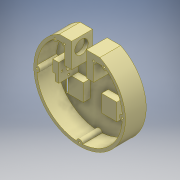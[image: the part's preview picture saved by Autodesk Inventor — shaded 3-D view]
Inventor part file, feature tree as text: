
AUTODESK INVENTOR PART (.ipt)
format: ipt  version: 2016 (Build 200138000, 138)  size: 337,920 bytes
history: native  units: mm
features: extrude x13, sketch x13, other x1
ambient origin geometry x8: Origin, YZ Plane, XZ Plane, XY Plane, X Axis, Y Axis, Z Axis, Center Point
bodies: Body1 (feature_tree)
feature tree (27):
  other  "Sólido1"
  extrude  "Extrusión1"  Depth=18.0mm
  extrude  "Extrusión2"  Depth=15.0mm
  extrude  "Extrusión3"  Depth=15.0mm
  extrude  "Extrusión4"  Depth=40.0mm
  extrude  "Extrusión5"  Depth=2.0mm TaperAngle=0.0deg
  extrude  "Extrusión6"  Depth=140.0mm
  extrude  "Extrusión8"  Depth=25.0mm
  extrude  "Extrusión9"  Depth=25.0mm
  extrude  "Extrusión10"  Depth=11.0mm TaperAngle=0.0deg
  extrude  "Extrusión11"  Depth=32.0mm TaperAngle=0.0deg
  extrude  "Extrusión12"  Depth=22.0mm
  extrude  "Extrusión13"  Depth=38.0mm TaperAngle=0.0deg
  extrude  "Extrusión14"  Depth=10.0mm
  sketch  "Boceto1"  dims[d0=150.0mm d2=18.0mm]
  sketch  "Boceto2"  dims[d3=25.0mm d4=15.0mm]
  sketch  "Boceto3"  dims[d5=50.0mm d6=15.0mm]
  sketch  "Boceto4"  dims[d7=50.0mm d8=40.0mm]
  sketch  "Boceto5"  dims[d9=40.0mm d12=2.0mm d13=0.0mm]
  sketch  "Boceto6"  dims[d14=150.0mm d23=140.0mm]
  sketch  "Boceto8"  dims[d25=32.0mm d26=0.0mm d27=25.0mm]
  sketch  "Boceto9"  dims[d28=28.0mm d30=25.0mm]
  sketch  "Boceto10"  dims[d31=28.0mm d33=11.0mm d34=0.0mm]
  sketch  "Boceto11"  dims[d37=21.0mm d38=32.0mm d39=0.0mm]
  sketch  "Boceto12"  dims[d40=22.0mm d41=21.0mm]
  sketch  "Boceto13"  dims[d42=18.0mm d43=38.0mm d44=0.0mm]
  sketch  "Boceto14"  dims[d45=10.0mm d46=10.0mm d47=10.0mm d48=3.0mm d49=3.0mm d50=3.0mm d51=33.0mm d52=0.0mm d63=8.0mm d64=8.0mm d65=11.0mm d66=11.0mm d67=15.0mm d69=70.0mm d70=0.0mm d71=5.0mm d72=140.0mm d73=12.0mm d76=10.0mm d77=12.0mm d78=10.0mm d79=32.0mm d80=0.0mm d81=8.0mm d82=8.0mm d83=8.0mm d84=8.0mm d85=32.0mm d86=0.0mm d89=3.0mm d90=3.0mm d91=3.0mm d92=3.0mm d93=32.0mm d94=0.0mm d95=8.0mm d96=16.0mm d97=15.0mm d98=3.0mm d99=5.0mm d102=3.0mm d103=5.0mm d104=3.0mm d105=5.0mm d106=3.0mm d107=16.0mm d108=16.0mm d109=15.0mm d110=23.5mm d111=50.0mm d112=0.0mm d116=32.0mm d117=0.0mm d118=3.0mm d119=4.0mm d120=12.0mm d121=3.0mm d122=4.0mm d123=20.0mm d124=29.0mm d125=0.0mm]
